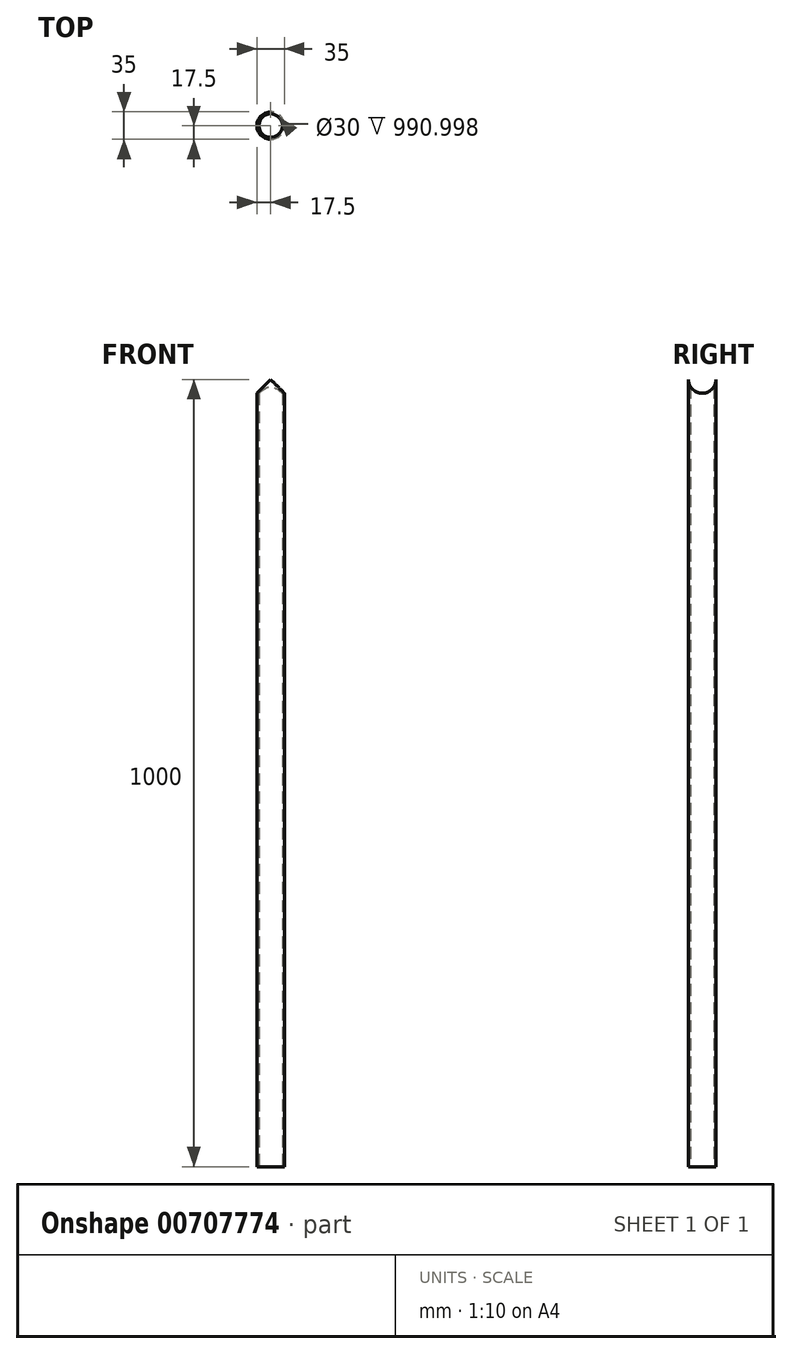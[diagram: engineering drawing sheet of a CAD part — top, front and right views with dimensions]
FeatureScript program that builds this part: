
annotation { "Feature Type Name" : "Feature", "Feature Type Description" : "" }
export const myFeature = defineFeature(function(context is Context, id is Id, definition is map)
    precondition{}
    {
        {
            var Q0;
            Q0=qCreatedBy(makeId("Top.planeOp"),FACE);
            var sketch = newSketch(context, id + "F0", { "sketchPlane" : qUnion([Q0])});
            skCircle(sketch, "E0", {"center": v(0, 0) * mm, "radius": 15 * mm});
            skCircle(sketch, "E1", {"center": v(0, 0) * mm, "radius": 17.5 * mm});
            skSolve(sketch);
        }
        {
            var Q0;
            Q0=makeQuery(id+"F0.imprint","IMPRINT",FACE,{"disambiguationData":[TD([[makeQuery(id+"F0.imprint","IMPRINT",EDGE,{"derivedFrom":sQuery(id+"F0.wireOp",EDGE,"E0")}),-1.0]])]});
            extrude(context, id + "F1", {"entities" : qUnion([Q0]), "depth" : 1000 * mm, "offsetDistance" : 25.4 * mm});
        }
        {
            var Q0;
            Q0=qCreatedBy(makeId("Right.planeOp"),FACE);
            var sketch = newSketch(context, id + "F2", { "sketchPlane" : qUnion([Q0])});
            skCircle(sketch, "E2", {"center": v(0, 1000) * mm, "radius": 17.5 * mm});
            skLineSegment(sketch, "E3.0", {"start": v(-17.5, 1000) * mm, "end": v(17.5, 1000) * mm, "construction": true});
            skSolve(sketch);
        }
        {
            var Q0;
            Q0=makeQuery(id+"F2.imprint","IMPRINT",FACE,{"disambiguationData":[TD([[makeQuery(id+"F2.imprint","IMPRINT",EDGE,{"derivedFrom":sQuery(id+"F2.wireOp",EDGE,"E2")}),1.0]])]});
            extrude(context, id + "F3", {"entities" : qUnion([Q0]), "operationType" : NewBodyOperationType.REMOVE, "endBound" : BoundingType.SYMMETRIC, "depth" : 50 * mm, "offsetDistance" : 25.4 * mm});
        }
    });
